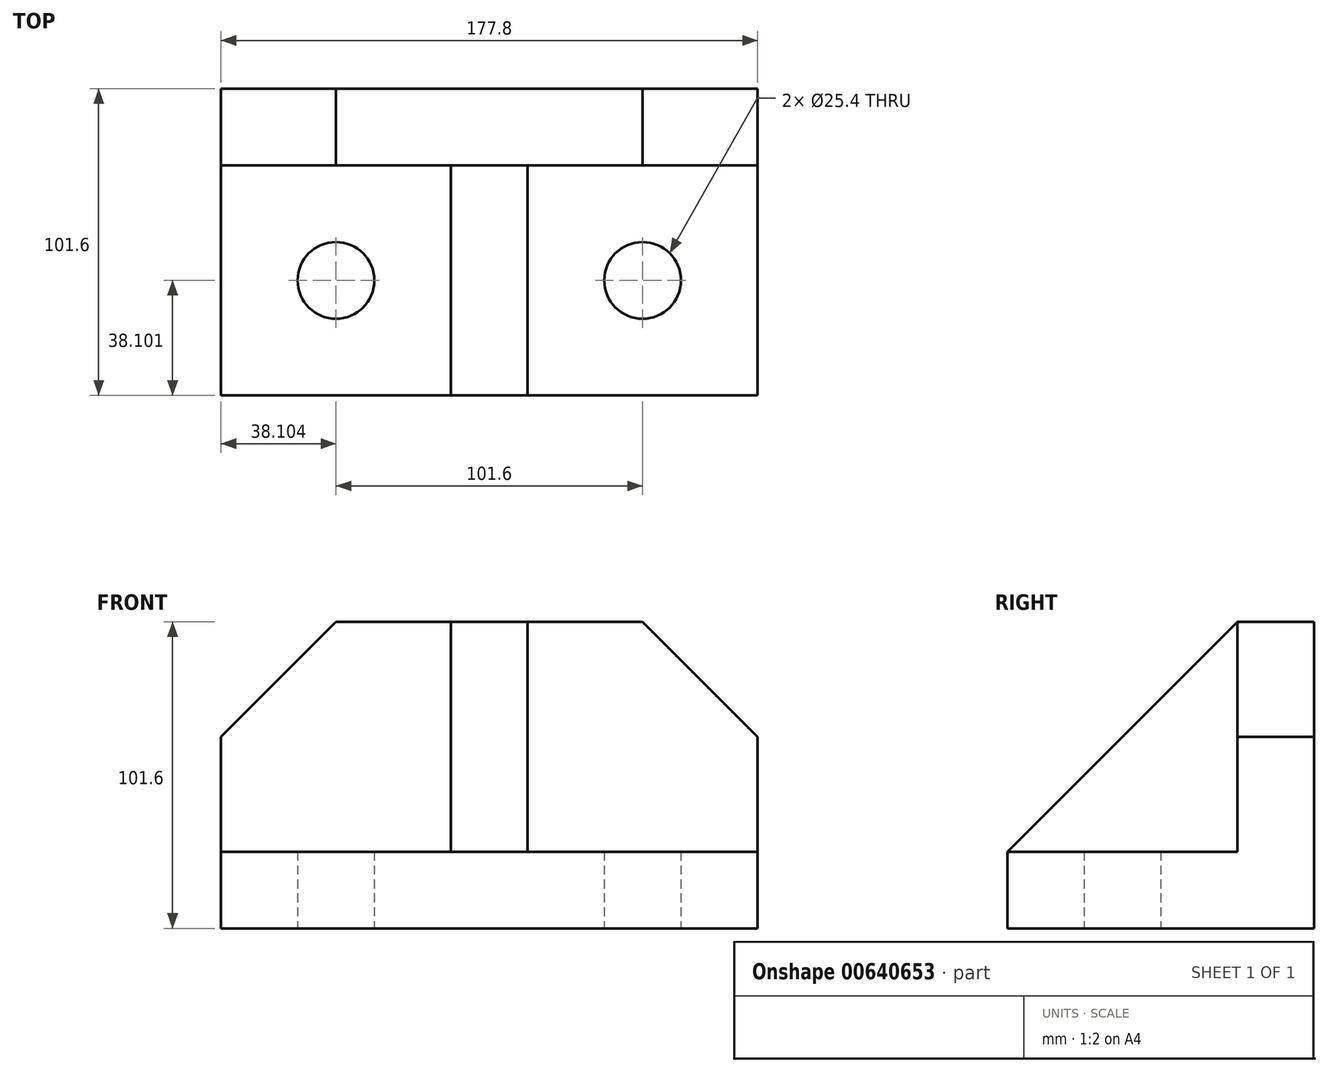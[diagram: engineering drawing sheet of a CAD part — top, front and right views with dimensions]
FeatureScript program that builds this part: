
annotation { "Feature Type Name" : "Feature", "Feature Type Description" : "" }
export const myFeature = defineFeature(function(context is Context, id is Id, definition is map)
    precondition{}
    {
        {
            var Q0;
            Q0=qCreatedBy(makeId("Top.planeOp"),FACE);
            var sketch = newSketch(context, id + "F0", { "sketchPlane" : qUnion([Q0])});
            skLineSegment(sketch, "E0.bottom", {"start": v(-96.49, 60.92) * mm, "end": v(81.31, 60.92) * mm});
            skLineSegment(sketch, "E0.top", {"start": v(-96.49, -40.68) * mm, "end": v(81.31, -40.68) * mm});
            skLineSegment(sketch, "E0.left", {"start": v(-96.49, 60.92) * mm, "end": v(-96.49, -40.68) * mm});
            skLineSegment(sketch, "E0.right", {"start": v(81.31, 60.92) * mm, "end": v(81.31, -40.68) * mm});
            skLineSegment(sketch, "E1", {"start": v(-20.29, 60.92) * mm, "end": v(-20.29, -40.68) * mm});
            skLineSegment(sketch, "E2", {"start": v(5.11, 60.92) * mm, "end": v(5.11, -40.68) * mm});
            skLineSegment(sketch, "E3", {"start": v(-96.49, 35.52) * mm, "end": v(-20.29, 35.52) * mm});
            skLineSegment(sketch, "E4", {"start": v(5.11, 35.52) * mm, "end": v(81.31, 35.52) * mm});
            skCircle(sketch, "E5", {"center": v(-58.39, -2.58) * mm, "radius": 12.7 * mm});
            skCircle(sketch, "E6", {"center": v(43.21, -2.58) * mm, "radius": 12.7 * mm});
            skSolve(sketch);
        }
        {
            var Q0;
            Q0 = qSketchRegion(id + "F0", true);
            extrude(context, id + "F1", {"entities" : qUnion([Q0]), "depth" : 25.4 * mm, "offsetDistance" : 25.4 * mm});
        }
        {
            var Q0;
            Q0=makeQuery(id+"F1.opExtrude","CAP_FACE",FACE,{"disambiguationData":[OSD([sQuery(id+"F0.wireOp",EDGE,"E0.bottom"),sQuery(id+"F0.wireOp",EDGE,"E0.top"),sQuery(id+"F0.wireOp",EDGE,"E0.left"),sQuery(id+"F0.wireOp",EDGE,"E0.right"),sQuery(id+"F0.wireOp",EDGE,"E5"),sQuery(id+"F0.wireOp",EDGE,"E6")])],"isStart":false});
            var sketch = newSketch(context, id + "F2", { "sketchPlane" : qUnion([Q0])});
            skLineSegment(sketch, "E7", {"start": v(-96.49, 35.52) * mm, "end": v(81.31, 35.52) * mm});
            skLineSegment(sketch, "E8", {"start": v(-20.29, 35.52) * mm, "end": v(-20.29, 60.92) * mm});
            skLineSegment(sketch, "E9", {"start": v(5.11, 35.52) * mm, "end": v(5.11, 60.92) * mm});
            skLineSegment(sketch, "E10", {"start": v(-20.29, 35.52) * mm, "end": v(-20.29, -40.68) * mm});
            skLineSegment(sketch, "E11", {"start": v(5.11, 35.52) * mm, "end": v(5.11, -40.68) * mm});
            skLineSegment(sketch, "E12", {"start": v(-96.49, 35.52) * mm, "end": v(-96.49, 60.92) * mm});
            skLineSegment(sketch, "E13", {"start": v(-96.49, 60.92) * mm, "end": v(81.31, 60.92) * mm});
            skLineSegment(sketch, "E14", {"start": v(81.31, 60.92) * mm, "end": v(81.31, 35.52) * mm});
            skLineSegment(sketch, "E15", {"start": v(30.51, 35.52) * mm, "end": v(30.51, 60.92) * mm});
            skLineSegment(sketch, "E16", {"start": v(-45.69, 35.52) * mm, "end": v(-45.69, 60.92) * mm});
            skSolve(sketch);
        }
        {
            var Q0;
            {var subQ0=sQuery(id+"F2.wireOp",EDGE,"E14");Q0=makeQuery(id+"F2.imprint","IMPRINT",FACE,{"disambiguationData":[TD([[makeQuery(id+"F2.imprint","IMPRINT",EDGE,{"derivedFrom":subQ0}),-1.0]])]});}
            var Q1;
            {var subQ0=sQuery(id+"F2.wireOp",EDGE,"E8");Q1=makeQuery(id+"F2.imprint","IMPRINT",FACE,{"disambiguationData":[TD([[makeQuery(id+"F2.imprint","IMPRINT",EDGE,{"derivedFrom":subQ0}),1.0]])]});}
            var Q2;
            {var subQ0=sQuery(id+"F2.wireOp",EDGE,"E8");Q2=makeQuery(id+"F2.imprint","IMPRINT",FACE,{"disambiguationData":[TD([[makeQuery(id+"F2.imprint","IMPRINT",EDGE,{"derivedFrom":subQ0}),-1.0]])]});}
            var Q3;
            {var subQ0=sQuery(id+"F2.wireOp",EDGE,"E9");Q3=makeQuery(id+"F2.imprint","IMPRINT",FACE,{"disambiguationData":[TD([[makeQuery(id+"F2.imprint","IMPRINT",EDGE,{"derivedFrom":subQ0}),-1.0]])]});}
            var Q4;
            {var subQ0=sQuery(id+"F2.wireOp",EDGE,"E12");Q4=makeQuery(id+"F2.imprint","IMPRINT",FACE,{"disambiguationData":[TD([[makeQuery(id+"F2.imprint","IMPRINT",EDGE,{"derivedFrom":subQ0}),1.0]])]});}
            var Q5;
            {var subQ0=sQuery(id+"F2.wireOp",EDGE,"E10");Q5=makeQuery(id+"F2.imprint","IMPRINT",FACE,{"disambiguationData":[TD([[makeQuery(id+"F2.imprint","IMPRINT",EDGE,{"derivedFrom":subQ0}),1.0]])]});}
            extrude(context, id + "F3", {"entities" : qUnion([Q0, Q1, Q2, Q3, Q4, Q5]), "operationType" : NewBodyOperationType.ADD, "depth" : 76.2 * mm, "offsetDistance" : 25.4 * mm});
        }
        {
            var Q0;
            Q0=makeQuery(id+"F3.opExtrude","CAP_EDGE",EDGE,{"disambiguationData":[OSD([sQuery(id+"F0.wireOp",EDGE,"E0.top")])],"isStart":false});
            chamfer(context, id + "F4", {"entities" : qUnion([Q0]), "width" : 76.2 * mm, "tangentPropagation" : true});
        }
        {
            var Q0;
            Q0=makeQuery(id+"F3.opExtrude","CAP_EDGE",EDGE,{"disambiguationData":[OSD([sQuery(id+"F2.wireOp",EDGE,"E14")])],"isStart":false});
            var Q1;
            Q1=makeQuery(id+"F3.opExtrude","CAP_EDGE",EDGE,{"disambiguationData":[OSD([sQuery(id+"F2.wireOp",EDGE,"E12")])],"isStart":false});
            chamfer(context, id + "F5", {"entities" : qUnion([Q0, Q1]), "width" : 38.1 * mm, "tangentPropagation" : true});
        }
    });
